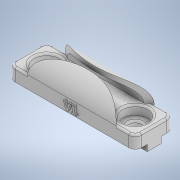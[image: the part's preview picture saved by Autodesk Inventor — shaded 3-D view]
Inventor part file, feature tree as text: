
AUTODESK INVENTOR PART (.ipt)
format: ipt  version: 2020 (Build 240168000, 168)  size: 265,728 bytes
history: native  units: in
note: dims shown in document units (in); Inventor stores cm internally (conversion verified against a paired STEP export)
features: sketch x6, extrude x4, fillet x2, hole x1, emboss x1
ambient origin geometry x8: Origin, YZ Plane, XZ Plane, XY Plane, X Axis, Y Axis, Z Axis, Center Point
bodies: Solid1 (feature_tree)
feature tree (14):
  extrude  "Extrusion1"  Depth=0.6in
  extrude  "Extrusion2"  Depth=0.2in
  hole  "Hole1"  [1 undecoded]
  extrude  "Extrusion3"  Depth=0.3in
  extrude  "Extrusion4"  Depth=0.3in
  fillet  "Fillet2"  Radius=0.1in
  emboss  "Emboss1"
  fillet  "Fillet3"  Radius=0.3in
  sketch  "Sketch1"  dims[d0=2.0in d1=0.6in]
  sketch  "Sketch2"  dims[d2=0.2in d3=0.0in d4=0.11in]
  sketch  "Sketch3"  dims[d5=0.11in d6=0.1in d7=0.0in]
  sketch  "Sketch4"  dims[d8=0.3in d9=0.3in]
  sketch  "Sketch5"  dims[d10=0.2in d11=0.75in d12=0.4in d13=0.15in d14=0.5635in d15=1.0in d16=0.8108in d17=0.05in d18=0.1in d19=0.3in d20=0.0in]
  sketch  "Sketch6"  dims[d22=0.07in d23=0.07in d24=0.07in d25=2.0in d26=0.0in d27=0.1in d28=0.03in d29=0.0in d30=0.03in]
note: 1 required parameter value undecoded (feature->parameter linkage not recoverable at this tier; creation-order binding heuristic only, values carry confidence <= 0.55)
